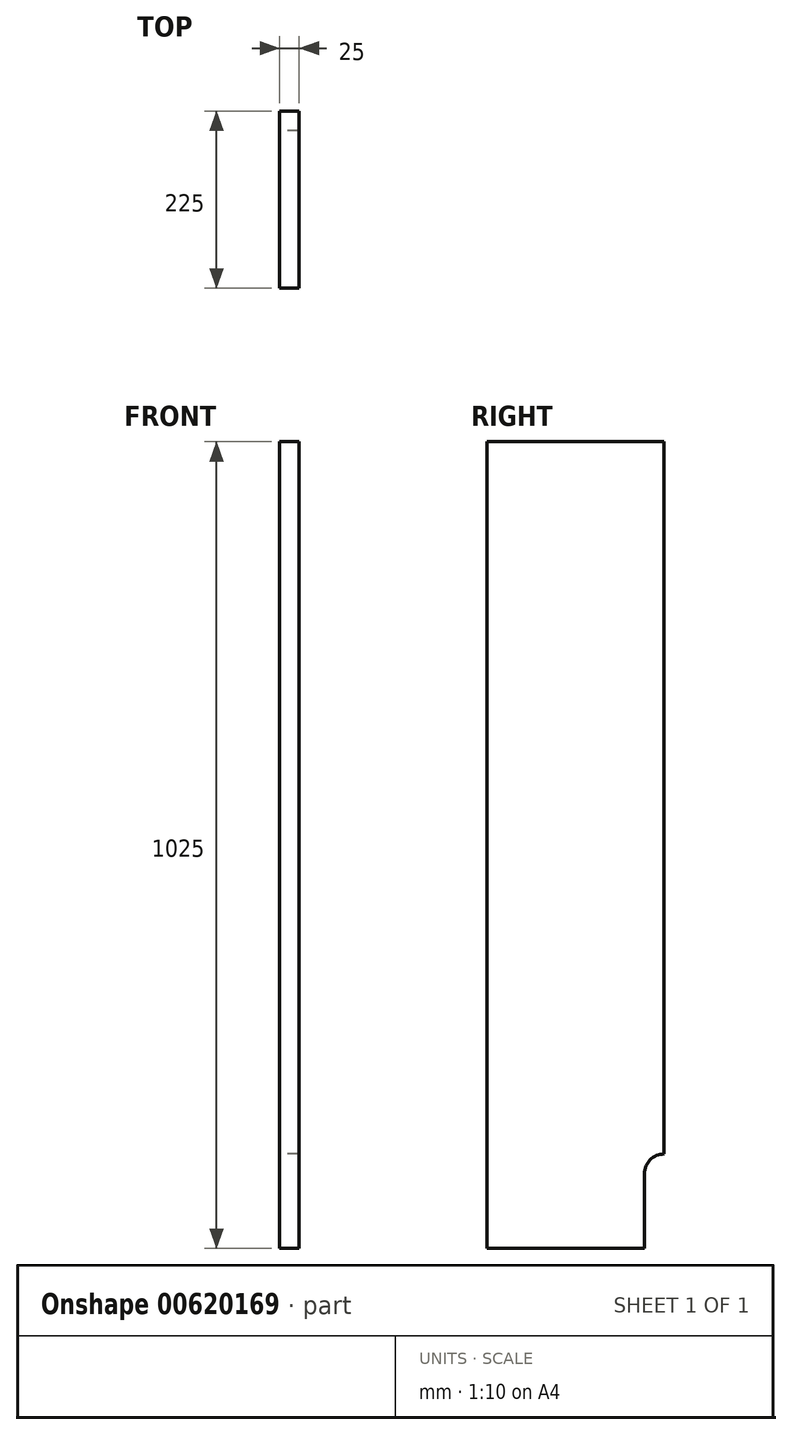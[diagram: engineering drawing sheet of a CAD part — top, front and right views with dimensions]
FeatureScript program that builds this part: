
annotation { "Feature Type Name" : "Feature", "Feature Type Description" : "" }
export const myFeature = defineFeature(function(context is Context, id is Id, definition is map)
    precondition{}
    {
        {
            var Q0;
            Q0=qCreatedBy(makeId("Right.planeOp"),FACE);
            var sketch = newSketch(context, id + "F0", { "sketchPlane" : qUnion([Q0])});
            skLineSegment(sketch, "E0.bottom", {"start": v(0, 512.5) * mm, "end": v(-225, 512.5) * mm});
            skLineSegment(sketch, "E0.top", {"start": v(-25, -512.5) * mm, "end": v(-225, -512.5) * mm});
            skLineSegment(sketch, "E0.left", {"start": v(0, 512.5) * mm, "end": v(0, -392.5) * mm});
            skLineSegment(sketch, "E0.right", {"start": v(-225, 512.5) * mm, "end": v(-225, -512.5) * mm});
            skPoint(sketch, "E0.middle", {"position": v(-112.5, 0) * mm});
            skLineSegment(sketch, "E1", {"start": v(-25, -417.5) * mm, "end": v(-25, -512.5) * mm});
            skArc(sketch, "E2", {"start": v(-25, -417.5) * mm, "mid": v(-17.68, -399.82) * mm, "end": v(0, -392.5) * mm});
            skPoint(sketch, "E3.orphan", {"position": v(0, -512.5) * mm});
            skSolve(sketch);
        }
        {
            var Q0;
            Q0=makeQuery(id+"F0.imprint","IMPRINT",FACE,{"disambiguationData":[TD([[makeQuery(id+"F0.imprint","IMPRINT",EDGE,{"derivedFrom":sQuery(id+"F0.wireOp",EDGE,"E0.bottom")}),1.0]])]});
            extrude(context, id + "F1", {"entities" : qUnion([Q0]), "depth" : 25 * mm, "offsetDistance" : 25 * mm});
        }
    });
